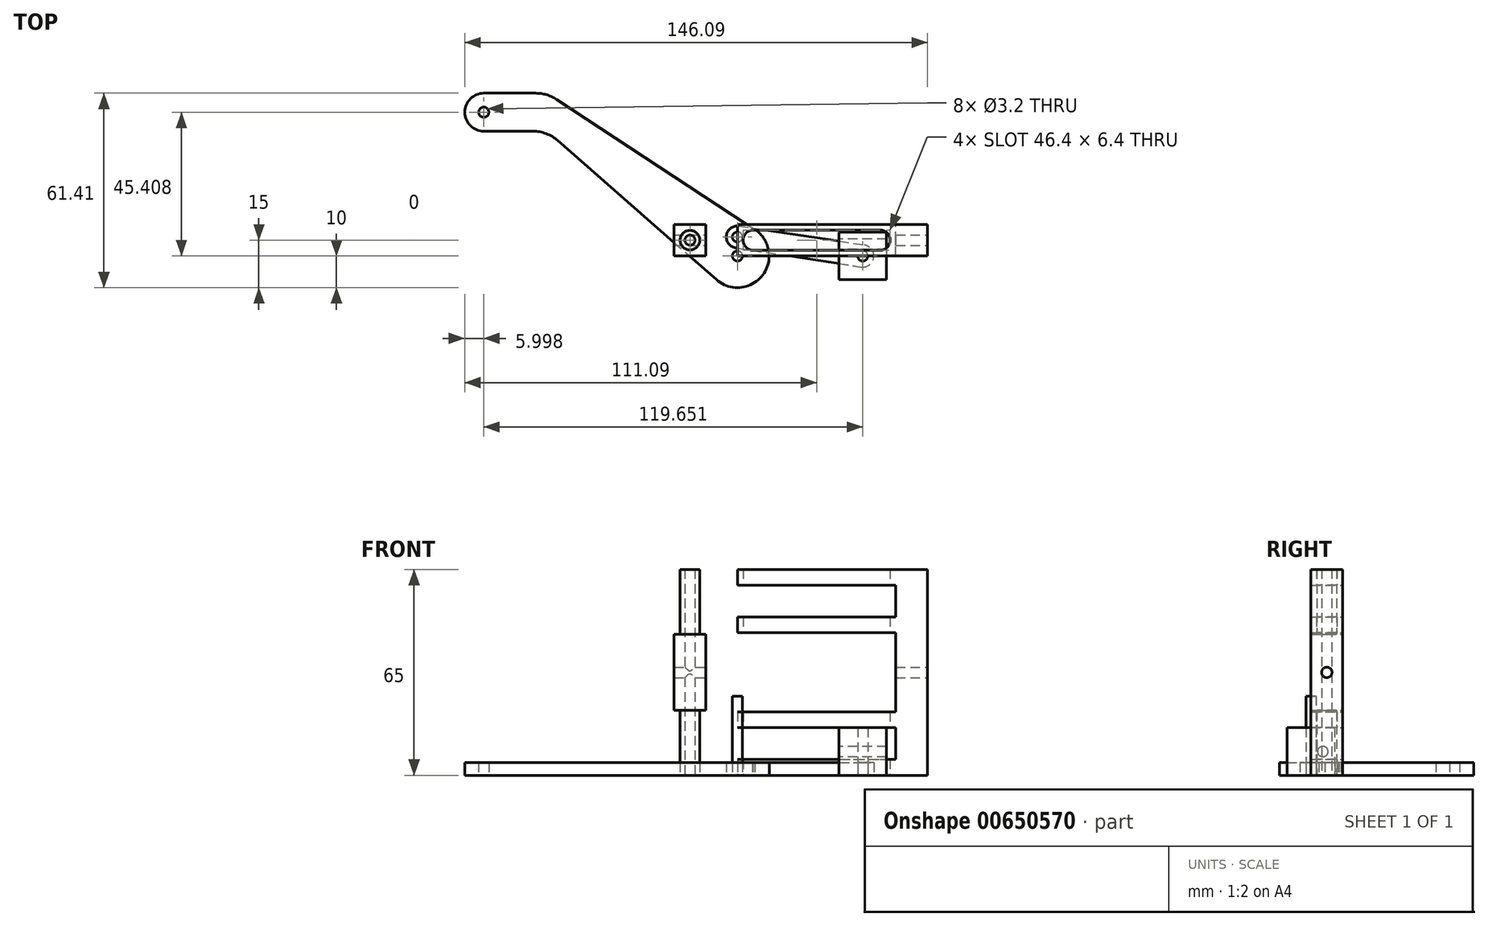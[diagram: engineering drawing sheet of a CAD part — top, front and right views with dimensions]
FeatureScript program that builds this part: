
annotation { "Feature Type Name" : "Feature", "Feature Type Description" : "" }
export const myFeature = defineFeature(function(context is Context, id is Id, definition is map)
    precondition{}
    {
        {
            var Q0;
            Q0=qCreatedBy(makeId("Top.planeOp"),FACE);
            var sketch = newSketch(context, id + "F0", { "sketchPlane" : qUnion([Q0])});
            skLineSegment(sketch, "E0.bottom", {"start": v(0, 0) * mm, "end": v(60, 0) * mm});
            skLineSegment(sketch, "E0.top", {"start": v(0, 10) * mm, "end": v(60, 10) * mm});
            skLineSegment(sketch, "E0.left", {"start": v(0, 0) * mm, "end": v(0, 10) * mm});
            skLineSegment(sketch, "E0.right", {"start": v(60, 0) * mm, "end": v(60, 10) * mm});
            skCircle(sketch, "E1", {"center": v(-15, 5) * mm, "radius": 1.6 * mm});
            skCircle(sketch, "E2.0", {"center": v(-15, 5) * mm, "radius": 3.1 * mm});
            skCircle(sketch, "E3", {"center": v(5, 5) * mm, "radius": 3.2 * mm});
            skPoint(sketch, "E4", {"position": v(0, 5) * mm});
            skCircle(sketch, "E5", {"center": v(45, 5) * mm, "radius": 3.2 * mm});
            skLineSegment(sketch, "E6", {"start": v(5, 8.2) * mm, "end": v(45, 8.2) * mm});
            skLineSegment(sketch, "E7", {"start": v(5, 1.8) * mm, "end": v(45, 1.8) * mm});
            skLineSegment(sketch, "E8.right", {"start": v(50, 0) * mm, "end": v(50, 10) * mm});
            skLineSegment(sketch, "E9.bottom", {"start": v(-20, 0) * mm, "end": v(-10, 0) * mm});
            skLineSegment(sketch, "E9.top", {"start": v(-20, 10) * mm, "end": v(-10, 10) * mm});
            skLineSegment(sketch, "E9.left", {"start": v(-20, 0) * mm, "end": v(-20, 10) * mm});
            skLineSegment(sketch, "E9.right", {"start": v(-10, 0) * mm, "end": v(-10, 10) * mm});
            skPoint(sketch, "E10", {"position": v(-15, 10) * mm});
            skSolve(sketch);
        }
        {
            var Q0;
            {var subQ0=sQuery(id+"F0.wireOp",EDGE,"E0.right");Q0=makeQuery(id+"F0.imprint","IMPRINT",FACE,{"disambiguationData":[TD([[makeQuery(id+"F0.imprint","IMPRINT",EDGE,{"derivedFrom":subQ0}),1.0]])]});}
            extrude(context, id + "F1", {"entities" : qUnion([Q0]), "depth" : 65 * mm, "offsetDistance" : 25 * mm});
        }
        {
            var Q0;
            {var subQ3=sQuery(id+"F0.wireOp",EDGE,"E0.left");Q0=makeQuery(id+"F0.imprint","IMPRINT",FACE,{"disambiguationData":[TD([[makeQuery(id+"F0.imprint","IMPRINT",EDGE,{"derivedFrom":subQ3}),-1.0]])]});}
            var Q1;
            {var subQ0=sQuery(id+"F0.wireOp",EDGE,"E0.right");Q1=makeQuery(id+"F0.imprint","IMPRINT",FACE,{"disambiguationData":[TD([[makeQuery(id+"F0.imprint","IMPRINT",EDGE,{"derivedFrom":subQ0}),1.0]])]});}
            extrude(context, id + "F2", {"entities" : qUnion([Q0, Q1]), "operationType" : NewBodyOperationType.ADD, "depth" : 5 * mm, "offsetDistance" : 25 * mm});
        }
        {
            var Q0;
            {var subQ3=sQuery(id+"F0.wireOp",EDGE,"E0.left");Q0=makeQuery(id+"F0.imprint","IMPRINT",FACE,{"disambiguationData":[TD([[makeQuery(id+"F0.imprint","IMPRINT",EDGE,{"derivedFrom":subQ3}),-1.0]])]});}
            var Q1;
            {var subQ0=sQuery(id+"F0.wireOp",EDGE,"E0.right");Q1=makeQuery(id+"F0.imprint","IMPRINT",FACE,{"disambiguationData":[TD([[makeQuery(id+"F0.imprint","IMPRINT",EDGE,{"derivedFrom":subQ0}),1.0]])]});}
            extrude(context, id + "F3", {"entities" : qUnion([Q0, Q1]), "operationType" : NewBodyOperationType.ADD, "depth" : 20 * mm, "offsetDistance" : 25 * mm, "hasSecondDirection" : true, "secondDirectionOppositeDirection" : false, "secondDirectionDepth" : 15 * mm});
        }
        {
            var Q0;
            {var subQ3=sQuery(id+"F0.wireOp",EDGE,"E0.left");Q0=makeQuery(id+"F0.imprint","IMPRINT",FACE,{"disambiguationData":[TD([[makeQuery(id+"F0.imprint","IMPRINT",EDGE,{"derivedFrom":subQ3}),-1.0]])]});}
            var Q1;
            {var subQ0=sQuery(id+"F0.wireOp",EDGE,"E0.right");Q1=makeQuery(id+"F0.imprint","IMPRINT",FACE,{"disambiguationData":[TD([[makeQuery(id+"F0.imprint","IMPRINT",EDGE,{"derivedFrom":subQ0}),1.0]])]});}
            extrude(context, id + "F4", {"entities" : qUnion([Q0, Q1]), "operationType" : NewBodyOperationType.ADD, "depth" : 50 * mm, "offsetDistance" : 25 * mm, "hasSecondDirection" : true, "secondDirectionOppositeDirection" : false, "secondDirectionDepth" : 45 * mm});
        }
        {
            var Q0;
            {var subQ3=sQuery(id+"F0.wireOp",EDGE,"E0.left");Q0=makeQuery(id+"F0.imprint","IMPRINT",FACE,{"disambiguationData":[TD([[makeQuery(id+"F0.imprint","IMPRINT",EDGE,{"derivedFrom":subQ3}),-1.0]])]});}
            var Q1;
            {var subQ0=sQuery(id+"F0.wireOp",EDGE,"E0.right");Q1=makeQuery(id+"F0.imprint","IMPRINT",FACE,{"disambiguationData":[TD([[makeQuery(id+"F0.imprint","IMPRINT",EDGE,{"derivedFrom":subQ0}),1.0]])]});}
            extrude(context, id + "F5", {"entities" : qUnion([Q0, Q1]), "operationType" : NewBodyOperationType.ADD, "depth" : 65 * mm, "offsetDistance" : 25 * mm, "hasSecondDirection" : true, "secondDirectionOppositeDirection" : false, "secondDirectionDepth" : 60 * mm});
        }
        {
            var Q0;
            Q0=makeQuery(id+"F0.imprint","IMPRINT",FACE,{"disambiguationData":[TD([[makeQuery(id+"F0.imprint","IMPRINT",EDGE,{"derivedFrom":sQuery(id+"F0.wireOp",EDGE,"E1")}),-1.0]])]});
            extrude(context, id + "F6", {"entities" : qUnion([Q0]), "depth" : 65 * mm, "offsetDistance" : 25 * mm});
        }
        {
            var Q0;
            Q0=makeQuery(id+"F0.imprint","IMPRINT",FACE,{"disambiguationData":[TD([[makeQuery(id+"F0.imprint","IMPRINT",EDGE,{"derivedFrom":sQuery(id+"F0.wireOp",EDGE,"E2.0")}),-1.0]])]});
            extrude(context, id + "F7", {"entities" : qUnion([Q0]), "operationType" : NewBodyOperationType.ADD, "depth" : 44.5 * mm, "offsetDistance" : 25 * mm, "hasSecondDirection" : true, "secondDirectionOppositeDirection" : false, "secondDirectionDepth" : 20.5 * mm});
        }
        {
            var Q0;
            Q0=makeQuery(id+"F7.opExtrude","SWEPT_FACE",FACE,{"disambiguationData":[OSD([sQuery(id+"F0.wireOp",EDGE,"E9.left")])]});
            var sketch = newSketch(context, id + "F8", { "sketchPlane" : qUnion([Q0])});
            skLineSegment(sketch, "E11", {"start": v(0, 44.5) * mm, "end": v(-10, 20.5) * mm, "construction": true});
            skLineSegment(sketch, "E12", {"start": v(-10, 44.5) * mm, "end": v(0, 20.5) * mm, "construction": true});
            skPoint(sketch, "E13", {"position": v(-5, 32.5) * mm});
            skSolve(sketch);
        }
        {
            var Q0;
            Q0=sQuery(id+"F8.wireOp",VERTEX,"E13");
            var Q1;
            Q1=makeQuery(id+"F1.opExtrude","SWEPT_BODY",BODY,{"disambiguationData":[OSD([sQuery(id+"F0.wireOp",EDGE,"E0.bottom"),sQuery(id+"F0.wireOp",EDGE,"E0.top"),sQuery(id+"F0.wireOp",EDGE,"E0.right"),sQuery(id+"F0.wireOp",EDGE,"E8.right")])]});
            var Q2;
            Q2=makeQuery(id+"F6.opExtrude","SWEPT_BODY",BODY,{"disambiguationData":[OSD([sQuery(id+"F0.wireOp",EDGE,"E1"),sQuery(id+"F0.wireOp",EDGE,"E2.0")])]});
            hole(context, id + "F9", {"style" : HoleStyle.SIMPLE, "endStyle" : HoleEndStyle.THROUGH, "standardTappedOrClearance" : lookupTablePath({ "standard" : "ISO", "fit" : "Normal", "size" : "M3", "type" : "Clearance" }), "standardBlindInLast" : lookupTablePath({ "fit" : "Standard", "standard" : "ISO", "size" : "M3", "type" : "Clearance" }), "holeDiameter" : 3.3 * mm, "majorDiameter" : 5 * mm, "isTappedThrough" : true, "tappedDepth" : 12 * mm, "tapClearance" : 3, "locations" : qUnion([Q0]), "scope" : qUnion([Q1, Q2])});
        }
        {
            var Q0;
            Q0=qCreatedBy(makeId("Top.planeOp"),FACE);
            var sketch = newSketch(context, id + "F10", { "sketchPlane" : qUnion([Q0])});
            skCircle(sketch, "E14", {"center": v(0, 0) * mm, "radius": 10 * mm});
            skCircle(sketch, "E15", {"center": v(0, 6) * mm, "radius": 1.6 * mm});
            skCircle(sketch, "E16", {"center": v(-80.1, 45.4) * mm, "radius": 1.6 * mm});
            skCircle(sketch, "E17", {"center": v(-80.1, 45.4) * mm, "radius": 6 * mm});
            skLineSegment(sketch, "E18", {"start": v(-80.1, 51.4) * mm, "end": v(-60.1, 51.4) * mm});
            skLineSegment(sketch, "E19", {"start": v(-80.1, 39.4) * mm, "end": v(-60.1, 39.4) * mm});
            skLineSegment(sketch, "E20", {"start": v(-60.1, 39.4) * mm, "end": v(-6.6, -7.52) * mm});
            skLineSegment(sketch, "E21", {"start": v(-60.1, 51.4) * mm, "end": v(5.49, 8.36) * mm});
            skCircle(sketch, "E22", {"center": v(0, 0) * mm, "radius": 1.6 * mm});
            skCircle(sketch, "E23", {"center": v(0, 6) * mm, "radius": 3.5 * mm});
            skCircle(sketch, "E24", {"center": v(39.56, 0) * mm, "radius": 3.5 * mm});
            skLineSegment(sketch, "E25", {"start": v(0.52, 9.46) * mm, "end": v(40.08, 3.46) * mm});
            skLineSegment(sketch, "E26", {"start": v(0, 2.5) * mm, "end": v(39.03, -3.46) * mm});
            skLineSegment(sketch, "E27.bottom", {"start": v(32.06, 7.5) * mm, "end": v(47.06, 7.5) * mm});
            skLineSegment(sketch, "E27.top", {"start": v(32.06, -7.5) * mm, "end": v(47.06, -7.5) * mm});
            skLineSegment(sketch, "E27.left", {"start": v(32.06, 7.5) * mm, "end": v(32.06, -7.5) * mm});
            skLineSegment(sketch, "E27.right", {"start": v(47.06, 7.5) * mm, "end": v(47.06, -7.5) * mm});
            skCircle(sketch, "E28", {"center": v(39.56, 0) * mm, "radius": 1.6 * mm});
            skSolve(sketch);
        }
        {
            var Q0;
            {var subQ1=sQuery(id+"F10.wireOp",EDGE,"E18");Q0=makeQuery(id+"F10.imprint","IMPRINT",FACE,{"disambiguationData":[TD([[makeQuery(id+"F10.imprint","IMPRINT",EDGE,{"derivedFrom":subQ1}),-1.0]])]});}
            var Q1;
            Q1=makeQuery(id+"F10.imprint","IMPRINT",FACE,{"disambiguationData":[TD([[makeQuery(id+"F10.imprint","IMPRINT",EDGE,{"derivedFrom":sQuery(id+"F10.wireOp",EDGE,"E16")}),-1.0]])]});
            var Q2;
            Q2=makeQuery(id+"F10.imprint","IMPRINT",FACE,{"disambiguationData":[TD([[makeQuery(id+"F10.imprint","IMPRINT",EDGE,{"derivedFrom":sQuery(id+"F10.wireOp",EDGE,"E22")}),-1.0]])]});
            var Q3;
            {var subQ3=sQuery(id+"F10.wireOp",EDGE,"E14");var subQ5=makeQuery(id+"F10.imprint","INTERSECT",VERTEX,{"derivedFrom":[subQ3,sQuery(id+"F10.wireOp",EDGE,"E21")]});Q3=makeQuery(id+"F10.imprint","IMPRINT",FACE,{"disambiguationData":[TD([[makeQuery(id+"F10.imprint","IMPRINT",EDGE,{"disambiguationData":[TD([[subQ5,1.0]])],"derivedFrom":subQ3}),1.0]])]});}
            var Q4;
            Q4=makeQuery(id+"F10.imprint","IMPRINT",FACE,{"disambiguationData":[TD([[makeQuery(id+"F10.imprint","IMPRINT",EDGE,{"derivedFrom":sQuery(id+"F10.wireOp",EDGE,"E15")}),-1.0]])]});
            extrude(context, id + "F11", {"entities" : qUnion([Q0, Q1, Q2, Q3, Q4]), "depth" : 4 * mm, "offsetDistance" : 25 * mm});
        }
        {
            var Q0;
            {var subQ1=sQuery(id+"F10.wireOp",EDGE,"E14");var subQ5=sQuery(id+"F10.wireOp",EDGE,"E21");var subQ6=makeQuery(id+"F10.imprint","INTERSECT",VERTEX,{"derivedFrom":[subQ1,subQ5]});Q0=makeQuery(id+"F10.imprint","IMPRINT",FACE,{"disambiguationData":[TD([[makeQuery(id+"F10.imprint","IMPRINT",EDGE,{"disambiguationData":[TD([[subQ6,1.0]])],"derivedFrom":subQ1}),-1.0]])]});}
            var Q1;
            {var subQ3=sQuery(id+"F10.wireOp",EDGE,"E14");var subQ5=makeQuery(id+"F10.imprint","INTERSECT",VERTEX,{"derivedFrom":[subQ3,sQuery(id+"F10.wireOp",EDGE,"E21")]});Q1=makeQuery(id+"F10.imprint","IMPRINT",FACE,{"disambiguationData":[TD([[makeQuery(id+"F10.imprint","IMPRINT",EDGE,{"disambiguationData":[TD([[subQ5,1.0]])],"derivedFrom":subQ3}),1.0]])]});}
            var Q2;
            Q2=makeQuery(id+"F10.imprint","IMPRINT",FACE,{"disambiguationData":[TD([[makeQuery(id+"F10.imprint","IMPRINT",EDGE,{"derivedFrom":sQuery(id+"F10.wireOp",EDGE,"E15")}),-1.0]])]});
            var Q3;
            {var subQ0=sQuery(id+"F10.wireOp",EDGE,"E25");var subQ1=sQuery(id+"F10.wireOp",EDGE,"E24");var subQ2=makeQuery(id+"F10.imprint","INTERSECT",VERTEX,{"derivedFrom":[subQ1,subQ0]});Q3=makeQuery(id+"F10.imprint","IMPRINT",FACE,{"disambiguationData":[TD([[makeQuery(id+"F10.imprint","IMPRINT",EDGE,{"disambiguationData":[TD([[subQ2,-1.0]])],"derivedFrom":subQ1}),-1.0]])]});}
            var Q4;
            Q4=makeQuery(id+"F10.imprint","IMPRINT",FACE,{"disambiguationData":[TD([[makeQuery(id+"F10.imprint","IMPRINT",EDGE,{"derivedFrom":sQuery(id+"F10.wireOp",EDGE,"E28")}),-1.0]])]});
            extrude(context, id + "F12", {"entities" : qUnion([Q0, Q1, Q2, Q3, Q4]), "depth" : 4 * mm, "offsetDistance" : 25 * mm});
        }
        {
            var Q0;
            {var subQ0=sQuery(id+"F10.wireOp",EDGE,"E27.bottom");Q0=makeQuery(id+"F10.imprint","IMPRINT",FACE,{"disambiguationData":[TD([[makeQuery(id+"F10.imprint","IMPRINT",EDGE,{"derivedFrom":subQ0}),-1.0]])]});}
            var Q1;
            {var subQ0=sQuery(id+"F10.wireOp",EDGE,"E25");var subQ1=sQuery(id+"F10.wireOp",EDGE,"E24");var subQ2=makeQuery(id+"F10.imprint","INTERSECT",VERTEX,{"derivedFrom":[subQ1,subQ0]});Q1=makeQuery(id+"F10.imprint","IMPRINT",FACE,{"disambiguationData":[TD([[makeQuery(id+"F10.imprint","IMPRINT",EDGE,{"disambiguationData":[TD([[subQ2,-1.0]])],"derivedFrom":subQ1}),-1.0]])]});}
            var Q2;
            Q2=makeQuery(id+"F10.imprint","IMPRINT",FACE,{"disambiguationData":[TD([[makeQuery(id+"F10.imprint","IMPRINT",EDGE,{"derivedFrom":sQuery(id+"F10.wireOp",EDGE,"E28")}),-1.0]])]});
            extrude(context, id + "F13", {"entities" : qUnion([Q0, Q1, Q2]), "depth" : 15 * mm, "offsetDistance" : 25 * mm});
        }
        {
            var Q0;
            Q0=makeQuery(id+"F13.opExtrude","SWEPT_FACE",FACE,{"disambiguationData":[OSD([sQuery(id+"F10.wireOp",EDGE,"E27.right")])]});
            var sketch = newSketch(context, id + "F14", { "sketchPlane" : qUnion([Q0])});
            skPoint(sketch, "E29", {"position": v(3.75, 7.5) * mm});
            skSolve(sketch);
        }
        {
            var Q0;
            Q0=sQuery(id+"F14.wireOp",VERTEX,"E29");
            var Q1;
            Q1=makeQuery(id+"F13.opExtrude","SWEPT_BODY",BODY,{"disambiguationData":[OSD([sQuery(id+"F10.wireOp",EDGE,"E27.bottom"),sQuery(id+"F10.wireOp",EDGE,"E27.top"),sQuery(id+"F10.wireOp",EDGE,"E27.left"),sQuery(id+"F10.wireOp",EDGE,"E27.right"),sQuery(id+"F10.wireOp",EDGE,"E28")])]});
            hole(context, id + "F15", {"style" : HoleStyle.SIMPLE, "endStyle" : HoleEndStyle.THROUGH, "standardTappedOrClearance" : lookupTablePath({ "standard" : "ISO", "fit" : "Normal", "size" : "M3", "type" : "Clearance" }), "standardBlindInLast" : lookupTablePath({ "fit" : "Standard", "standard" : "ISO", "size" : "M3", "type" : "Clearance" }), "holeDiameter" : 3.3 * mm, "majorDiameter" : 5 * mm, "isTappedThrough" : true, "tappedDepth" : 12 * mm, "tapClearance" : 3, "locations" : qUnion([Q0]), "scope" : qUnion([Q1])});
        }
        {
            var Q0;
            Q0=makeQuery(id+"F10.imprint","IMPRINT",FACE,{"disambiguationData":[TD([[makeQuery(id+"F10.imprint","IMPRINT",EDGE,{"derivedFrom":sQuery(id+"F10.wireOp",EDGE,"E22")}),1.0]])]});
            extrude(context, id + "F16", {"entities" : qUnion([Q0]), "depth" : 25 * mm, "offsetDistance" : 25 * mm});
        }
        {
            var Q0;
            Q0=makeQuery(id+"F11.opExtrude","SWEPT_EDGE",EDGE,{"disambiguationData":[OSD([sQuery(id+"F10.wireOp",EDGE,"E18"),sQuery(id+"F10.wireOp",EDGE,"E21")])]});
            var Q1;
            Q1=makeQuery(id+"F11.opExtrude","SWEPT_EDGE",EDGE,{"disambiguationData":[OSD([sQuery(id+"F10.wireOp",EDGE,"E19"),sQuery(id+"F10.wireOp",EDGE,"E20")])]});
            fillet(context, id + "F17", {"entities" : qUnion([Q0, Q1]), "radius" : 12 * mm, "tangentPropagation" : true, "allowEdgeOverflow" : false});
        }
    });
